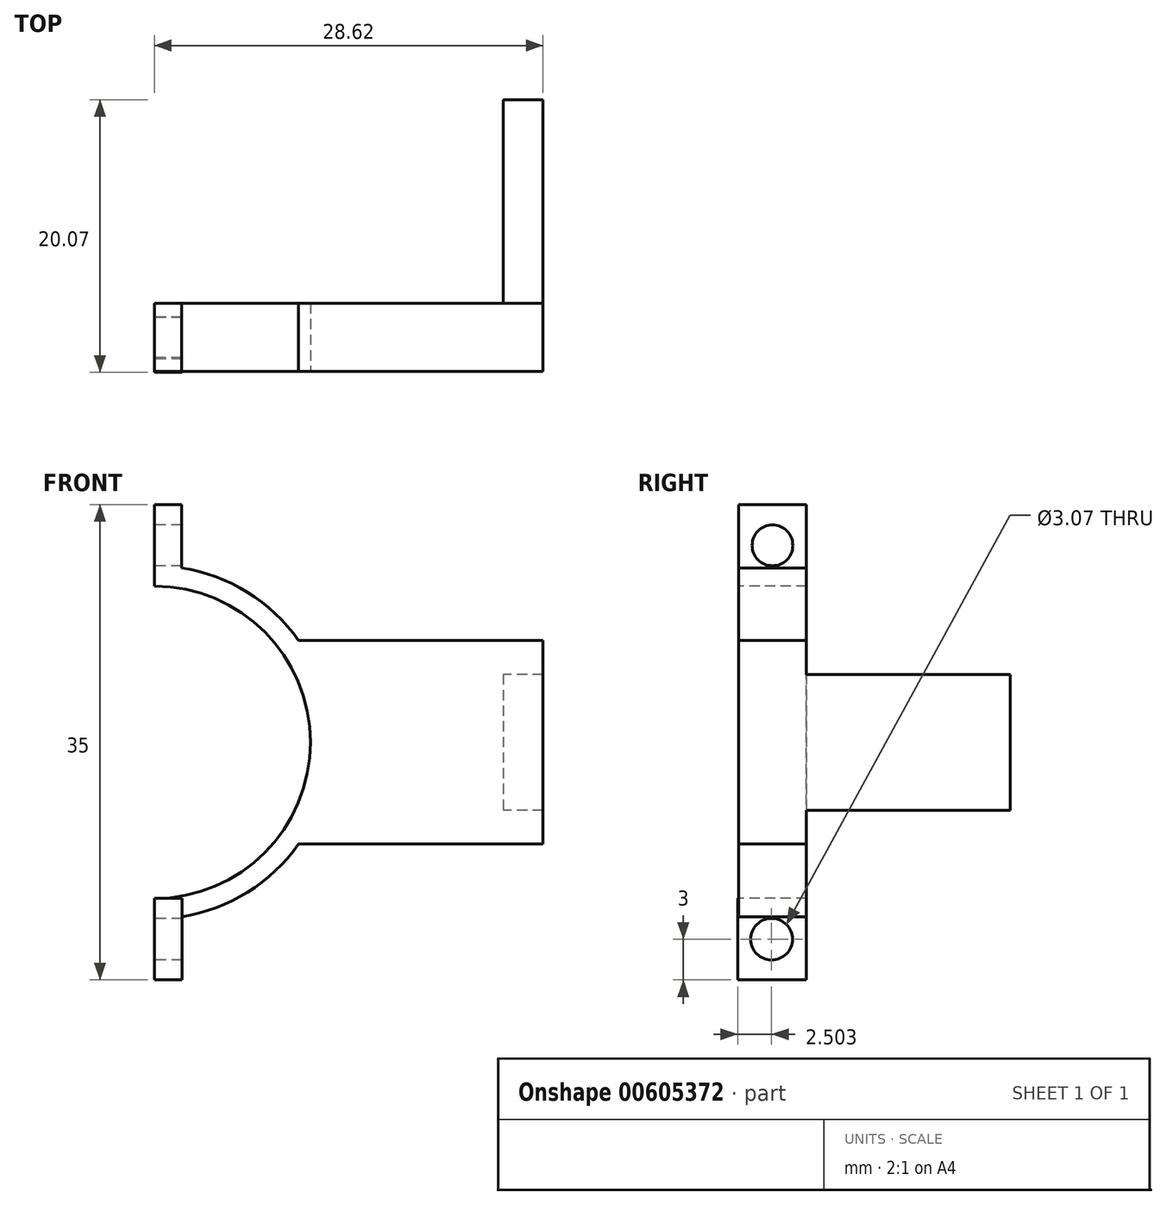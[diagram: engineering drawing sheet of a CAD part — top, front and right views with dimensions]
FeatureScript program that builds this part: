
annotation { "Feature Type Name" : "Feature", "Feature Type Description" : "" }
export const myFeature = defineFeature(function(context is Context, id is Id, definition is map)
    precondition{}
    {
        {
            var Q0;
            Q0=qCreatedBy(makeId("Front.planeOp"),FACE);
            var sketch = newSketch(context, id + "F0", { "sketchPlane" : qUnion([Q0])});
            skLineSegment(sketch, "E0", {"start": v(28.62, -7.5) * mm, "end": v(28.62, 7.5) * mm});
            skLineSegment(sketch, "E1", {"start": v(28.62, 7.5) * mm, "end": v(10.62, 7.5) * mm});
            skLineSegment(sketch, "E2", {"start": v(28.62, -7.5) * mm, "end": v(10.62, -7.5) * mm});
            skArc(sketch, "E3", {"start": v(10.62, 7.5) * mm, "mid": v(-13, 0) * mm, "end": v(10.62, -7.5) * mm});
            skSolve(sketch);
        }
        {
            var Q0;
            Q0=qSketchRegion(id+"F0",true);
            extrude(context, id + "F1", {"entities" : qUnion([Q0]), "depth" : 5 * mm, "offsetDistance" : 25 * mm});
        }
        {
            var Q0;
            Q0=makeQuery(id+"F1.opExtrude","CAP_FACE",FACE,{"disambiguationData":[OSD([sQuery(id+"F0.wireOp",EDGE,"E0"),sQuery(id+"F0.wireOp",EDGE,"E1"),sQuery(id+"F0.wireOp",EDGE,"E2"),sQuery(id+"F0.wireOp",EDGE,"E3")])],"isStart":false});
            var sketch = newSketch(context, id + "F2", { "sketchPlane" : qUnion([Q0])});
            skCircle(sketch, "E4", {"center": v(0, 0) * mm, "radius": 11.5 * mm});
            skSolve(sketch);
        }
        {
            var Q0;
            Q0=qSketchRegion(id+"F2",true);
            extrude(context, id + "F3", {"entities" : qUnion([Q0]), "operationType" : NewBodyOperationType.REMOVE, "oppositeDirection" : true, "depth" : 25 * mm, "offsetDistance" : 25 * mm});
        }
        {
            var Q0;
            Q0=makeQuery(id+"F1.opExtrude","SWEPT_FACE",FACE,{"disambiguationData":[OSD([sQuery(id+"F0.wireOp",EDGE,"E2")])]});
            var sketch = newSketch(context, id + "F4", { "sketchPlane" : qUnion([Q0])});
            skLineSegment(sketch, "E5.bottom", {"start": v(0, 13.24) * mm, "end": v(-19.72, 13.24) * mm});
            skLineSegment(sketch, "E5.top", {"start": v(0, -9.5) * mm, "end": v(-19.72, -9.5) * mm});
            skLineSegment(sketch, "E5.left", {"start": v(0, 13.24) * mm, "end": v(0, -9.5) * mm});
            skLineSegment(sketch, "E5.right", {"start": v(-19.72, 13.24) * mm, "end": v(-19.72, -9.5) * mm});
            skSolve(sketch);
        }
        {
            var Q0;
            Q0=qSketchRegion(id+"F4",true);
            extrude(context, id + "F5", {"entities" : qUnion([Q0]), "operationType" : NewBodyOperationType.REMOVE, "endBound" : BoundingType.THROUGH_ALL, "oppositeDirection" : true, "depth" : 25 * mm, "offsetDistance" : 25 * mm, "hasSecondDirection" : true, "secondDirectionOppositeDirection" : false, "secondDirectionDepth" : 50 * mm});
        }
        {
            var Q0;
            Q0=makeQuery(id+"F1.opExtrude","SWEPT_FACE",FACE,{"disambiguationData":[OSD([sQuery(id+"F0.wireOp",EDGE,"E2")])]});
            var sketch = newSketch(context, id + "F6", { "sketchPlane" : qUnion([Q0])});
            skLineSegment(sketch, "E6.bottom", {"start": v(0, 5.07) * mm, "end": v(2.04, 5.07) * mm});
            skLineSegment(sketch, "E6.top", {"start": v(0, 0) * mm, "end": v(2.04, 0) * mm});
            skLineSegment(sketch, "E6.left", {"start": v(0, 5.07) * mm, "end": v(0, 0) * mm});
            skLineSegment(sketch, "E6.right", {"start": v(2.04, 5.07) * mm, "end": v(2.04, 0) * mm});
            skSolve(sketch);
        }
        {
            var Q0;
            Q0=qSketchRegion(id+"F6",true);
            extrude(context, id + "F7", {"entities" : qUnion([Q0]), "operationType" : NewBodyOperationType.ADD, "depth" : 10 * mm, "offsetDistance" : 25 * mm, "hasSecondDirection" : true, "secondDirectionOppositeDirection" : false, "secondDirectionDepth" : 4 * mm});
        }
        {
            var Q0;
            Q0=makeQuery(id+"F7.boolean.opBoolean","MERGE",FACE,{"derivedFrom":[makeQuery(id+"F5.boolean.opBoolean","COPY",FACE,{"disambiguationData":[OD(1.0)],"derivedFrom":makeQuery(id+"F5.opExtrude","SWEPT_FACE",FACE,{"disambiguationData":[OSD([sQuery(id+"F4.wireOp",EDGE,"E5.left")])]})}),makeQuery(id+"F7.opExtrude","SWEPT_FACE",FACE,{"disambiguationData":[OSD([sQuery(id+"F6.wireOp",EDGE,"E6.left")])]})]});
            var sketch = newSketch(context, id + "F8", { "sketchPlane" : qUnion([Q0])});
            skCircle(sketch, "E7", {"center": v(2.57, -14.5) * mm, "radius": 1.54 * mm});
            skPoint(sketch, "E7.centerSnap0", {"position": v(0, -14.5) * mm});
            skSolve(sketch);
        }
        {
            var Q0;
            Q0=qSketchRegion(id+"F8",true);
            extrude(context, id + "F9", {"entities" : qUnion([Q0]), "operationType" : NewBodyOperationType.REMOVE, "oppositeDirection" : true, "depth" : 25 * mm, "offsetDistance" : 25 * mm});
        }
        {
            var Q0;
            Q0=makeQuery(id+"F7.boolean.opBoolean","MERGE",FACE,{"derivedFrom":[makeQuery(id+"F1.opExtrude","CAP_FACE",FACE,{"disambiguationData":[OSD([sQuery(id+"F0.wireOp",EDGE,"E0"),sQuery(id+"F0.wireOp",EDGE,"E1"),sQuery(id+"F0.wireOp",EDGE,"E2"),sQuery(id+"F0.wireOp",EDGE,"E3")])],"isStart":true}),makeQuery(id+"F7.opExtrude","SWEPT_FACE",FACE,{"disambiguationData":[OSD([sQuery(id+"F6.wireOp",EDGE,"E6.top")])]})]});
            var sketch = newSketch(context, id + "F10", { "sketchPlane" : qUnion([Q0])});
            skLineSegment(sketch, "E8.bottom", {"start": v(-28.7, 5) * mm, "end": v(-25.7, 5) * mm});
            skLineSegment(sketch, "E8.top", {"start": v(-28.7, -5) * mm, "end": v(-25.7, -5) * mm});
            skLineSegment(sketch, "E8.left", {"start": v(-28.7, 5) * mm, "end": v(-28.7, -5) * mm});
            skLineSegment(sketch, "E8.right", {"start": v(-25.7, 5) * mm, "end": v(-25.7, -5) * mm});
            skSolve(sketch);
        }
        {
            var Q0;
            {var subQ0=sQuery(id+"F10.wireOp",EDGE,"E8.right");Q0=makeQuery(id+"F10.imprint","IMPRINT",FACE,{"disambiguationData":[TD([[makeQuery(id+"F10.imprint","IMPRINT",EDGE,{"derivedFrom":subQ0}),-1.0]])]});}
            extrude(context, id + "F11", {"entities" : qUnion([Q0]), "operationType" : NewBodyOperationType.ADD, "depth" : 15 * mm, "offsetDistance" : 25 * mm});
        }
        {
            var Q0;
            Q0=makeQuery(id+"F1.opExtrude","SWEPT_FACE",FACE,{"disambiguationData":[OSD([sQuery(id+"F0.wireOp",EDGE,"E1")])]});
            var sketch = newSketch(context, id + "F12", { "sketchPlane" : qUnion([Q0])});
            skLineSegment(sketch, "E9.bottom", {"start": v(0, -5) * mm, "end": v(2, -5) * mm});
            skLineSegment(sketch, "E9.top", {"start": v(0, 0) * mm, "end": v(2, 0) * mm});
            skLineSegment(sketch, "E9.left", {"start": v(0, -5) * mm, "end": v(0, 0) * mm});
            skLineSegment(sketch, "E9.right", {"start": v(2, -5) * mm, "end": v(2, 0) * mm});
            skSolve(sketch);
        }
        {
            var Q0;
            Q0=qSketchRegion(id+"F12",true);
            extrude(context, id + "F13", {"entities" : qUnion([Q0]), "operationType" : NewBodyOperationType.ADD, "depth" : 10 * mm, "offsetDistance" : 25 * mm, "hasSecondDirection" : true, "secondDirectionOppositeDirection" : false, "secondDirectionDepth" : 4 * mm});
        }
        {
            var Q0;
            Q0=makeQuery(id+"F13.boolean.opBoolean","MERGE",FACE,{"derivedFrom":[makeQuery(id+"F5.boolean.opBoolean","COPY",FACE,{"disambiguationData":[OD(0.0)],"derivedFrom":makeQuery(id+"F5.opExtrude","SWEPT_FACE",FACE,{"disambiguationData":[OSD([sQuery(id+"F4.wireOp",EDGE,"E5.left")])]})}),makeQuery(id+"F13.opExtrude","SWEPT_FACE",FACE,{"disambiguationData":[OSD([sQuery(id+"F12.wireOp",EDGE,"E9.left")])]})]});
            var sketch = newSketch(context, id + "F14", { "sketchPlane" : qUnion([Q0])});
            skCircle(sketch, "E10", {"center": v(2.5, 14.5) * mm, "radius": 1.5 * mm});
            skSolve(sketch);
        }
        {
            var Q0;
            Q0=qSketchRegion(id+"F14",true);
            extrude(context, id + "F15", {"entities" : qUnion([Q0]), "operationType" : NewBodyOperationType.REMOVE, "oppositeDirection" : true, "depth" : 25 * mm, "offsetDistance" : 25 * mm});
        }
    });
